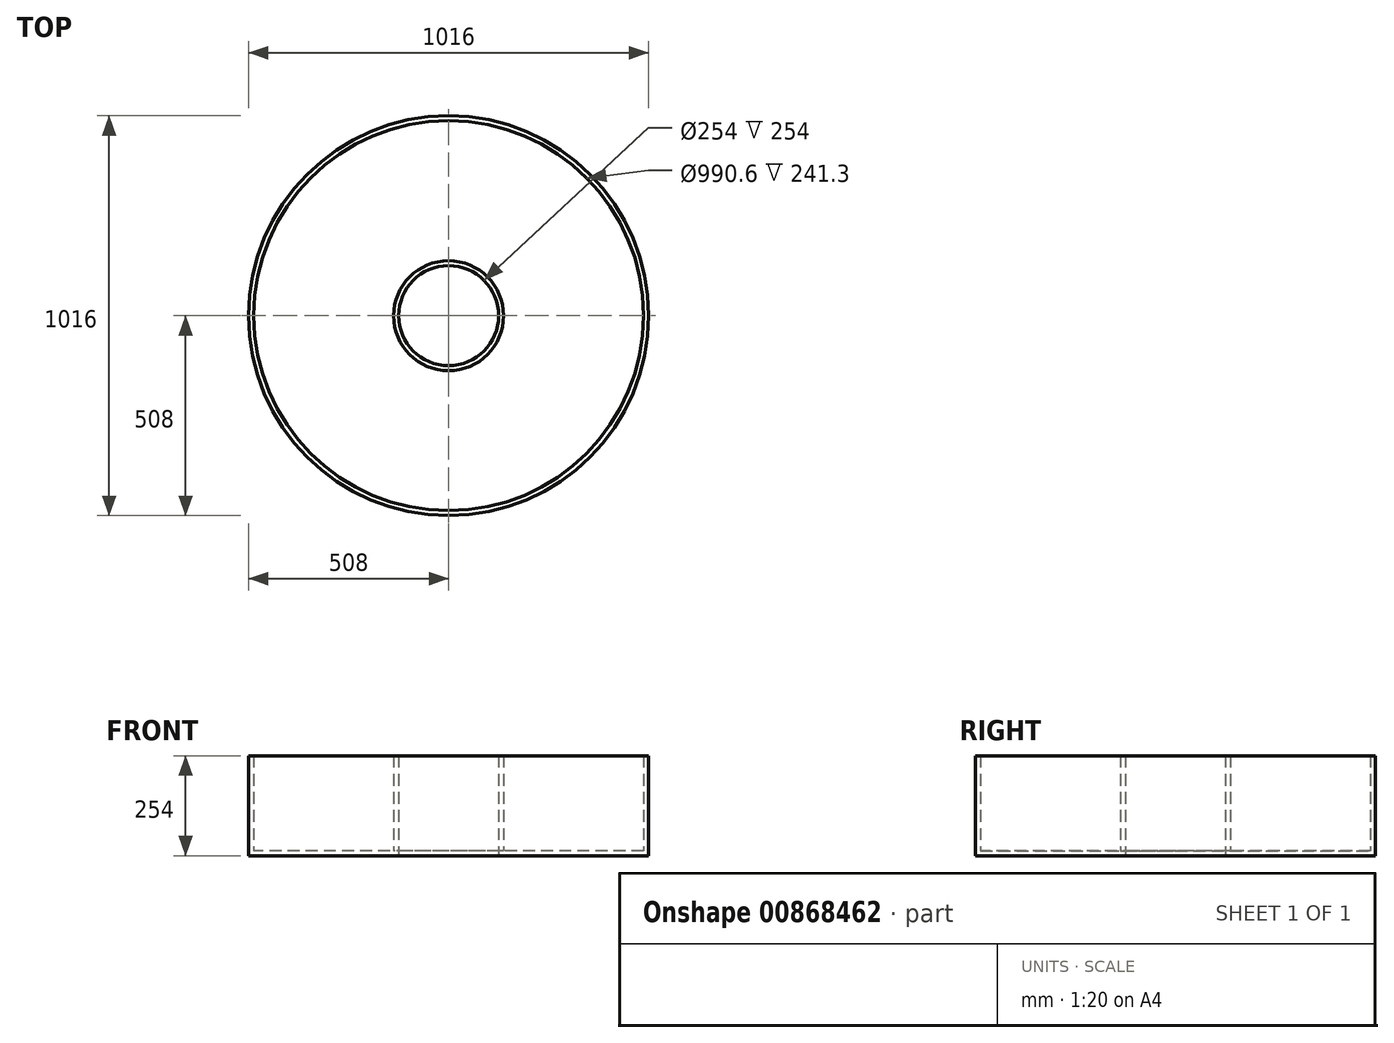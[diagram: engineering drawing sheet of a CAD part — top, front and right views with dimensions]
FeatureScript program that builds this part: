
annotation { "Feature Type Name" : "Feature", "Feature Type Description" : "" }
export const myFeature = defineFeature(function(context is Context, id is Id, definition is map)
    precondition{}
    {
        {
            var Q0;
            Q0=qCreatedBy(makeId("Top.planeOp"),FACE);
            var sketch = newSketch(context, id + "F0", { "sketchPlane" : qUnion([Q0])});
            skCircle(sketch, "E0", {"center": v(0, 0) * mm, "radius": 508 * mm});
            skCircle(sketch, "E1", {"center": v(0, 0) * mm, "radius": 127 * mm});
            skSolve(sketch);
        }
        {
            var Q0;
            Q0=makeQuery(id+"F0.imprint","IMPRINT",FACE,{"disambiguationData":[TD([[makeQuery(id+"F0.imprint","IMPRINT",EDGE,{"derivedFrom":sQuery(id+"F0.wireOp",EDGE,"E0")}),1.0]])]});
            extrude(context, id + "F1", {"entities" : qUnion([Q0]), "depth" : 254 * mm, "offsetDistance" : 25.4 * mm});
        }
        {
            var Q0;
            Q0=makeQuery(id+"F1.opExtrude","CAP_FACE",FACE,{"disambiguationData":[OSD([sQuery(id+"F0.wireOp",EDGE,"E0"),sQuery(id+"F0.wireOp",EDGE,"E1")])],"isStart":false});
            shell(context, id + "F2", {"entities" : qUnion([Q0]), "thickness" : 12.7 * mm});
        }
    });
